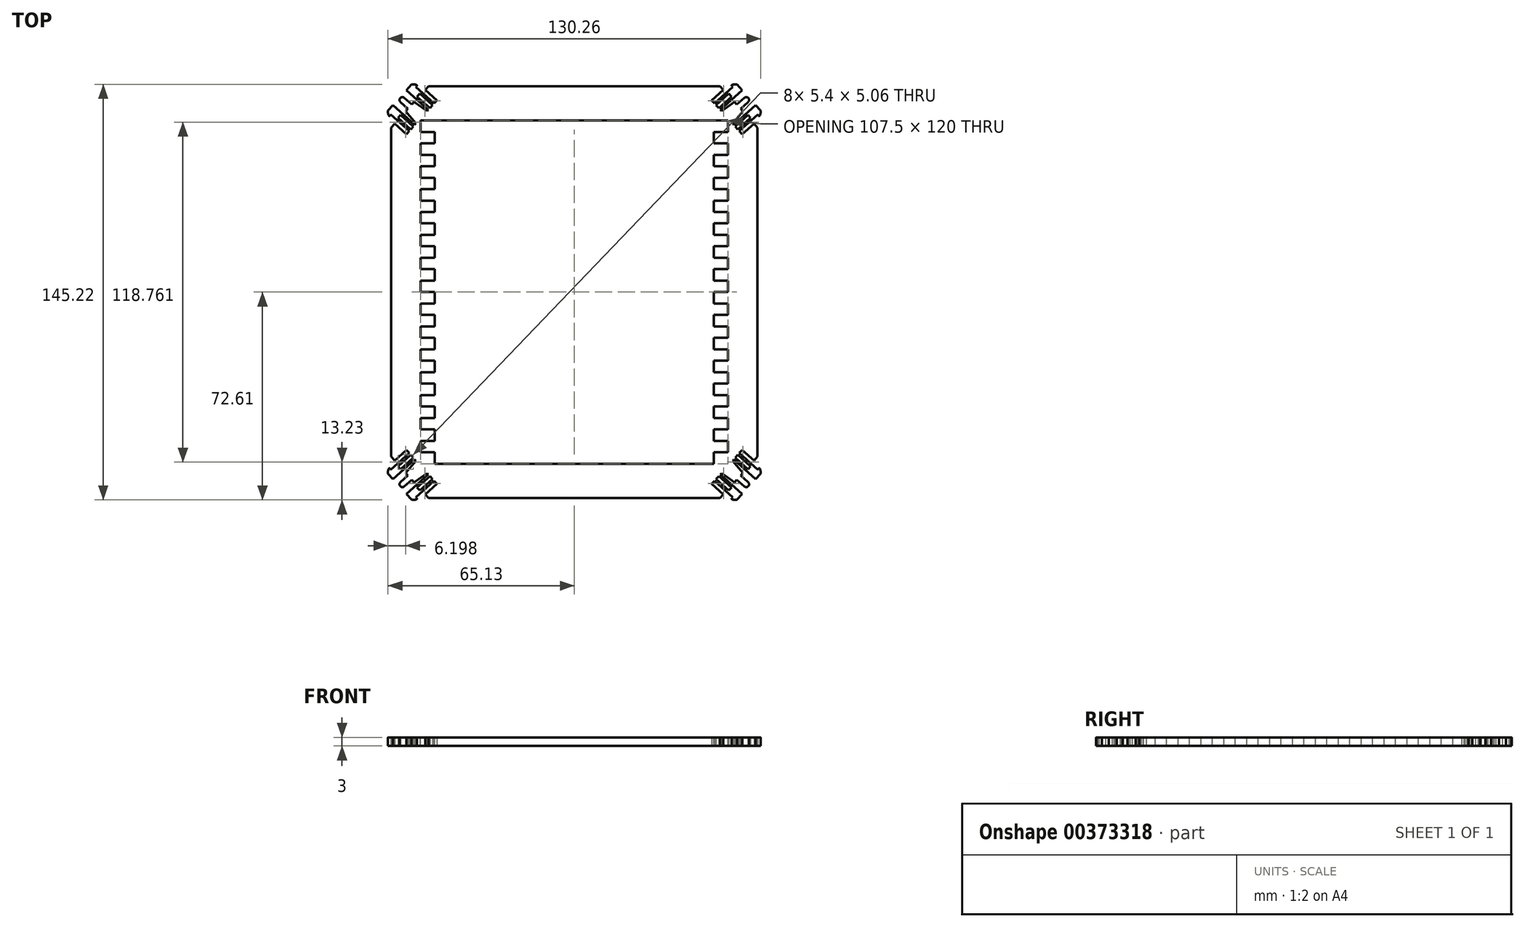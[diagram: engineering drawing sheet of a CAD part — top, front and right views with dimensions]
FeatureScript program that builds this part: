
annotation { "Feature Type Name" : "Feature", "Feature Type Description" : "" }
export const myFeature = defineFeature(function(context is Context, id is Id, definition is map)
    precondition{}
    {
        {
            var Q0;
            Q0=qCreatedBy(makeId("Top.planeOp"),FACE);
            var sketch = newSketch(context, id + "F0", { "sketchPlane" : qUnion([Q0])});
            skLineSegment(sketch, "E0", {"start": v(64, 57.49) * mm, "end": v(64, 0) * mm});
            skLineSegment(sketch, "E1", {"start": v(52.08, 70.72) * mm, "end": v(48, 67.04) * mm});
            skLineSegment(sketch, "E2", {"start": v(48, 67.04) * mm, "end": v(49, 65.92) * mm});
            skLineSegment(sketch, "E3", {"start": v(49, 65.92) * mm, "end": v(55.4, 71.67) * mm});
            skLineSegment(sketch, "E4", {"start": v(58.67, 70.58) * mm, "end": v(51.02, 63.69) * mm});
            skLineSegment(sketch, "E5", {"start": v(51.02, 63.69) * mm, "end": v(51.5, 63.29) * mm});
            skLineSegment(sketch, "E6", {"start": v(51.5, 63.29) * mm, "end": v(56, 66.46) * mm});
            skLineSegment(sketch, "E7", {"start": v(56, 66.46) * mm, "end": v(56.81, 65.55) * mm});
            skLineSegment(sketch, "E8", {"start": v(56.81, 65.55) * mm, "end": v(59.41, 67.89) * mm});
            skLineSegment(sketch, "E9", {"start": v(60.08, 67.15) * mm, "end": v(49.07, 57.23) * mm, "construction": true});
            skLineSegment(sketch, "E10.bottom", {"start": v(49.54, 65.32) * mm, "end": v(50.48, 64.28) * mm});
            skLineSegment(sketch, "E10.top", {"start": v(54, 69.34) * mm, "end": v(54.94, 68.3) * mm});
            skLineSegment(sketch, "E10.left", {"start": v(49.54, 65.32) * mm, "end": v(54, 69.34) * mm});
            skLineSegment(sketch, "E10.right", {"start": v(50.48, 64.28) * mm, "end": v(54.94, 68.3) * mm});
            skLineSegment(sketch, "E11", {"start": v(48, 67.04) * mm, "end": v(52.45, 62.1) * mm, "construction": true});
            skFitSpline(sketch, "E12", {"points": [v(55.4, 71.67) * mm, v(55, 72.26) * mm, v(56.93, 72.51) * mm], "startDerivative": vector(-1.28, 1.46) * mm, "endDerivative": vector(3.75, -1.07) * mm});
            skLineSegment(sketch, "E13", {"start": v(54.62, 75.08) * mm, "end": v(62.29, 66.57) * mm, "construction": true});
            skLineSegment(sketch, "E14", {"start": v(56.93, 72.51) * mm, "end": v(58.67, 70.58) * mm});
            skFitSpline(sketch, "E15.MirrorCS", {"points": [v(64.1, 62.01) * mm, v(64.64, 61.56) * mm, v(65.1, 63.45) * mm], "startDerivative": vector(1.32, -1.42) * mm, "endDerivative": vector(-0.67, 3.84) * mm});
            skLineSegment(sketch, "E16.MirrorCS", {"start": v(58.72, 55.14) * mm, "end": v(57.7, 56.26) * mm});
            skLineSegment(sketch, "E17.MirrorCS", {"start": v(57.17, 56.85) * mm, "end": v(56.23, 57.9) * mm});
            skLineSegment(sketch, "E18.MirrorCS", {"start": v(55.7, 58.49) * mm, "end": v(55.35, 59) * mm});
            skLineSegment(sketch, "E19.MirrorCS", {"start": v(58.72, 55.14) * mm, "end": v(54.27, 60.08) * mm, "construction": true});
            skLineSegment(sketch, "E20.MirrorCS", {"start": v(56.23, 57.9) * mm, "end": v(60.7, 61.9) * mm});
            skLineSegment(sketch, "E21.MirrorCS", {"start": v(62.8, 58.82) * mm, "end": v(58.72, 55.14) * mm});
            skLineSegment(sketch, "E22.MirrorCS", {"start": v(55.35, 59) * mm, "end": v(58.97, 63.15) * mm});
            skLineSegment(sketch, "E23.MirrorCS", {"start": v(63.35, 65.38) * mm, "end": v(55.7, 58.49) * mm});
            skLineSegment(sketch, "E24.MirrorCS", {"start": v(57.7, 56.26) * mm, "end": v(64.1, 62.01) * mm});
            skLineSegment(sketch, "E25.MirrorCS", {"start": v(65.1, 63.45) * mm, "end": v(63.35, 65.38) * mm});
            skLineSegment(sketch, "E26.MirrorCS", {"start": v(58.15, 64.06) * mm, "end": v(60.75, 66.4) * mm});
            skLineSegment(sketch, "E27.MirrorCS", {"start": v(61.63, 60.87) * mm, "end": v(60.7, 61.9) * mm});
            skLineSegment(sketch, "E28.MirrorCS", {"start": v(58.97, 63.15) * mm, "end": v(58.15, 64.06) * mm});
            skLineSegment(sketch, "E29.MirrorCS", {"start": v(57.17, 56.85) * mm, "end": v(61.63, 60.87) * mm});
            skArc(sketch, "E30", {"start": v(59.41, 67.89) * mm, "mid": v(60.83, 67.81) * mm, "end": v(60.75, 66.4) * mm});
            skLineSegment(sketch, "E31.0", {"start": v(54.62, 75.08) * mm, "end": v(56.93, 72.51) * mm, "construction": true});
            skLineSegment(sketch, "E32.0", {"start": v(51.5, 63.29) * mm, "end": v(52.45, 62.1) * mm, "construction": true});
            skLineSegment(sketch, "E33", {"start": v(50.93, 72) * mm, "end": v(0, 72) * mm});
            skLineSegment(sketch, "E34", {"start": v(0, 72) * mm, "end": v(0, 0) * mm});
            skLineSegment(sketch, "E35", {"start": v(0, 0) * mm, "end": v(64, 0) * mm});
            skLineSegment(sketch, "E36", {"start": v(52.08, 70.72) * mm, "end": v(50.93, 72) * mm});
            skLineSegment(sketch, "E37", {"start": v(62.8, 58.82) * mm, "end": v(64, 57.49) * mm});
            skSolve(sketch);
        }
        {
            var Q0;
            Q0=qSketchRegion(id+"F0",true);
            extrude(context, id + "F1", {"entities" : qUnion([Q0]), "depth" : 3 * mm});
        }
        {
            var Q0;
            Q0=makeQuery(id+"F1.opExtrude","SWEPT_BODY",BODY,{"disambiguationData":[OSD([sQuery(id+"F0.wireOp",EDGE,"E0"),sQuery(id+"F0.wireOp",EDGE,"E1"),sQuery(id+"F0.wireOp",EDGE,"E2"),sQuery(id+"F0.wireOp",EDGE,"E3"),sQuery(id+"F0.wireOp",EDGE,"E4"),sQuery(id+"F0.wireOp",EDGE,"E5"),sQuery(id+"F0.wireOp",EDGE,"E6"),sQuery(id+"F0.wireOp",EDGE,"E7"),sQuery(id+"F0.wireOp",EDGE,"E8"),sQuery(id+"F0.wireOp",EDGE,"E10.bottom"),sQuery(id+"F0.wireOp",EDGE,"E10.top"),sQuery(id+"F0.wireOp",EDGE,"E10.left"),sQuery(id+"F0.wireOp",EDGE,"E10.right"),sQuery(id+"F0.wireOp",EDGE,"E12"),sQuery(id+"F0.wireOp",EDGE,"E14"),sQuery(id+"F0.wireOp",EDGE,"E15.MirrorCS"),sQuery(id+"F0.wireOp",EDGE,"E16.MirrorCS"),sQuery(id+"F0.wireOp",EDGE,"E17.MirrorCS"),sQuery(id+"F0.wireOp",EDGE,"E18.MirrorCS"),sQuery(id+"F0.wireOp",EDGE,"73c64eb1-9053-4ded-a230-a61976290448.MirrorCS"),sQuery(id+"F0.wireOp",EDGE,"E20.MirrorCS"),sQuery(id+"F0.wireOp",EDGE,"E21.MirrorCS"),sQuery(id+"F0.wireOp",EDGE,"E22.MirrorCS"),sQuery(id+"F0.wireOp",EDGE,"E23.MirrorCS"),sQuery(id+"F0.wireOp",EDGE,"E24.MirrorCS"),sQuery(id+"F0.wireOp",EDGE,"E25.MirrorCS"),sQuery(id+"F0.wireOp",EDGE,"E26.MirrorCS"),sQuery(id+"F0.wireOp",EDGE,"E27.MirrorCS"),sQuery(id+"F0.wireOp",EDGE,"E28.MirrorCS"),sQuery(id+"F0.wireOp",EDGE,"E29.MirrorCS"),sQuery(id+"F0.wireOp",EDGE,"E30"),sQuery(id+"F0.wireOp",EDGE,"238d3171-18cf-4664-875a-15b81accc3c9"),sQuery(id+"F0.wireOp",EDGE,"7124a334-57a5-4c12-b1ba-874bc8632110.MirrorC"),sQuery(id+"F0.wireOp",EDGE,"E33"),sQuery(id+"F0.wireOp",EDGE,"44bece61-ac72-4aae-9b04-1ec5777349d3"),sQuery(id+"F0.wireOp",EDGE,"E34"),sQuery(id+"F0.wireOp",EDGE,"E35")])]});
            var Q1;
            Q1=makeQuery(id+"F1.opExtrude","SWEPT_FACE",FACE,{"disambiguationData":[OSD([sQuery(id+"F0.wireOp",EDGE,"E34")])]});
            mirror(context, id + "F2", {"operationType" : NewBodyOperationType.ADD, "entities" : qUnion([Q0]), "mirrorPlane" : qUnion([Q1])});
        }
        {
            var Q0;
            Q0=makeQuery(id+"F1.opExtrude","SWEPT_BODY",BODY,{"disambiguationData":[OSD([sQuery(id+"F0.wireOp",EDGE,"E0"),sQuery(id+"F0.wireOp",EDGE,"E1"),sQuery(id+"F0.wireOp",EDGE,"E2"),sQuery(id+"F0.wireOp",EDGE,"E3"),sQuery(id+"F0.wireOp",EDGE,"E4"),sQuery(id+"F0.wireOp",EDGE,"E5"),sQuery(id+"F0.wireOp",EDGE,"E6"),sQuery(id+"F0.wireOp",EDGE,"E7"),sQuery(id+"F0.wireOp",EDGE,"E8"),sQuery(id+"F0.wireOp",EDGE,"E10.bottom"),sQuery(id+"F0.wireOp",EDGE,"E10.top"),sQuery(id+"F0.wireOp",EDGE,"E10.left"),sQuery(id+"F0.wireOp",EDGE,"E10.right"),sQuery(id+"F0.wireOp",EDGE,"E12"),sQuery(id+"F0.wireOp",EDGE,"E14"),sQuery(id+"F0.wireOp",EDGE,"E15.MirrorCS"),sQuery(id+"F0.wireOp",EDGE,"E16.MirrorCS"),sQuery(id+"F0.wireOp",EDGE,"E17.MirrorCS"),sQuery(id+"F0.wireOp",EDGE,"E18.MirrorCS"),sQuery(id+"F0.wireOp",EDGE,"73c64eb1-9053-4ded-a230-a61976290448.MirrorCS"),sQuery(id+"F0.wireOp",EDGE,"E20.MirrorCS"),sQuery(id+"F0.wireOp",EDGE,"E21.MirrorCS"),sQuery(id+"F0.wireOp",EDGE,"E22.MirrorCS"),sQuery(id+"F0.wireOp",EDGE,"E23.MirrorCS"),sQuery(id+"F0.wireOp",EDGE,"E24.MirrorCS"),sQuery(id+"F0.wireOp",EDGE,"E25.MirrorCS"),sQuery(id+"F0.wireOp",EDGE,"E26.MirrorCS"),sQuery(id+"F0.wireOp",EDGE,"E27.MirrorCS"),sQuery(id+"F0.wireOp",EDGE,"E28.MirrorCS"),sQuery(id+"F0.wireOp",EDGE,"E29.MirrorCS"),sQuery(id+"F0.wireOp",EDGE,"E30"),sQuery(id+"F0.wireOp",EDGE,"238d3171-18cf-4664-875a-15b81accc3c9"),sQuery(id+"F0.wireOp",EDGE,"7124a334-57a5-4c12-b1ba-874bc8632110.MirrorC"),sQuery(id+"F0.wireOp",EDGE,"E33"),sQuery(id+"F0.wireOp",EDGE,"44bece61-ac72-4aae-9b04-1ec5777349d3"),sQuery(id+"F0.wireOp",EDGE,"E34"),sQuery(id+"F0.wireOp",EDGE,"E35")])]});
            var Q1;
            {var subQ0=makeQuery(id+"F1.opExtrude","SWEPT_FACE",FACE,{"disambiguationData":[OSD([sQuery(id+"F0.wireOp",EDGE,"E35")])]});Q1=makeQuery(id+"F2.boolean.opBoolean","MERGE",FACE,{"derivedFrom":[subQ0,makeQuery(id+"F2.opPattern","COPY",FACE,{"derivedFrom":subQ0,"instanceName":"1"})]});}
            mirror(context, id + "F3", {"operationType" : NewBodyOperationType.ADD, "entities" : qUnion([Q0]), "mirrorPlane" : qUnion([Q1])});
        }
        {
            var Q0;
            {var subQ0=makeQuery(id+"F1.opExtrude","CAP_FACE",FACE,{"disambiguationData":[OSD([sQuery(id+"F0.wireOp",EDGE,"E0"),sQuery(id+"F0.wireOp",EDGE,"E1"),sQuery(id+"F0.wireOp",EDGE,"E2"),sQuery(id+"F0.wireOp",EDGE,"E3"),sQuery(id+"F0.wireOp",EDGE,"E4"),sQuery(id+"F0.wireOp",EDGE,"E5"),sQuery(id+"F0.wireOp",EDGE,"E6"),sQuery(id+"F0.wireOp",EDGE,"E7"),sQuery(id+"F0.wireOp",EDGE,"E8"),sQuery(id+"F0.wireOp",EDGE,"E10.bottom"),sQuery(id+"F0.wireOp",EDGE,"E10.top"),sQuery(id+"F0.wireOp",EDGE,"E10.left"),sQuery(id+"F0.wireOp",EDGE,"E10.right"),sQuery(id+"F0.wireOp",EDGE,"E12"),sQuery(id+"F0.wireOp",EDGE,"E14"),sQuery(id+"F0.wireOp",EDGE,"E15.MirrorCS"),sQuery(id+"F0.wireOp",EDGE,"E16.MirrorCS"),sQuery(id+"F0.wireOp",EDGE,"E17.MirrorCS"),sQuery(id+"F0.wireOp",EDGE,"E18.MirrorCS"),sQuery(id+"F0.wireOp",EDGE,"73c64eb1-9053-4ded-a230-a61976290448.MirrorCS"),sQuery(id+"F0.wireOp",EDGE,"E20.MirrorCS"),sQuery(id+"F0.wireOp",EDGE,"E21.MirrorCS"),sQuery(id+"F0.wireOp",EDGE,"E22.MirrorCS"),sQuery(id+"F0.wireOp",EDGE,"E23.MirrorCS"),sQuery(id+"F0.wireOp",EDGE,"E24.MirrorCS"),sQuery(id+"F0.wireOp",EDGE,"E25.MirrorCS"),sQuery(id+"F0.wireOp",EDGE,"E26.MirrorCS"),sQuery(id+"F0.wireOp",EDGE,"E27.MirrorCS"),sQuery(id+"F0.wireOp",EDGE,"E28.MirrorCS"),sQuery(id+"F0.wireOp",EDGE,"E29.MirrorCS"),sQuery(id+"F0.wireOp",EDGE,"E30"),sQuery(id+"F0.wireOp",EDGE,"238d3171-18cf-4664-875a-15b81accc3c9"),sQuery(id+"F0.wireOp",EDGE,"7124a334-57a5-4c12-b1ba-874bc8632110.MirrorC"),sQuery(id+"F0.wireOp",EDGE,"E33"),sQuery(id+"F0.wireOp",EDGE,"44bece61-ac72-4aae-9b04-1ec5777349d3"),sQuery(id+"F0.wireOp",EDGE,"E34"),sQuery(id+"F0.wireOp",EDGE,"E35")])],"isStart":false});var subQ1=makeQuery(id+"F2.boolean.opBoolean","MERGE",FACE,{"derivedFrom":[subQ0,makeQuery(id+"F2.opPattern","COPY",FACE,{"derivedFrom":subQ0,"instanceName":"1"})]});Q0=makeQuery(id+"F3.boolean.opBoolean","MERGE",FACE,{"derivedFrom":[subQ1,makeQuery(id+"F3.opPattern","COPY",FACE,{"derivedFrom":subQ1,"instanceName":"1"})]});}
            var sketch = newSketch(context, id + "F4", { "sketchPlane" : qUnion([Q0])});
            skLineSegment(sketch, "E38.bottom", {"start": v(53.75, 60) * mm, "end": v(-53.75, 60) * mm});
            skLineSegment(sketch, "E38.top", {"start": v(53.75, -60) * mm, "end": v(-53.75, -60) * mm});
            skLineSegment(sketch, "E38.left", {"start": v(53.75, 60) * mm, "end": v(53.75, -60) * mm});
            skLineSegment(sketch, "E38.right", {"start": v(-53.75, 60) * mm, "end": v(-53.75, -60) * mm});
            skPoint(sketch, "E38.middle", {"position": v(0, 0) * mm});
            skSolve(sketch);
        }
        {
            var Q0;
            Q0=qSketchRegion(id+"F4",true);
            extrude(context, id + "F5", {"entities" : qUnion([Q0]), "operationType" : NewBodyOperationType.REMOVE, "oppositeDirection" : true, "depth" : 3 * mm});
        }
        {
            var Q0;
            {var subQ0=makeQuery(id+"F1.opExtrude","CAP_FACE",FACE,{"disambiguationData":[OSD([sQuery(id+"F0.wireOp",EDGE,"E0"),sQuery(id+"F0.wireOp",EDGE,"E1"),sQuery(id+"F0.wireOp",EDGE,"E2"),sQuery(id+"F0.wireOp",EDGE,"E3"),sQuery(id+"F0.wireOp",EDGE,"E4"),sQuery(id+"F0.wireOp",EDGE,"E5"),sQuery(id+"F0.wireOp",EDGE,"E6"),sQuery(id+"F0.wireOp",EDGE,"E7"),sQuery(id+"F0.wireOp",EDGE,"E8"),sQuery(id+"F0.wireOp",EDGE,"E10.bottom"),sQuery(id+"F0.wireOp",EDGE,"E10.top"),sQuery(id+"F0.wireOp",EDGE,"E10.left"),sQuery(id+"F0.wireOp",EDGE,"E10.right"),sQuery(id+"F0.wireOp",EDGE,"E12"),sQuery(id+"F0.wireOp",EDGE,"E14"),sQuery(id+"F0.wireOp",EDGE,"E15.MirrorCS"),sQuery(id+"F0.wireOp",EDGE,"E16.MirrorCS"),sQuery(id+"F0.wireOp",EDGE,"E17.MirrorCS"),sQuery(id+"F0.wireOp",EDGE,"E18.MirrorCS"),sQuery(id+"F0.wireOp",EDGE,"E20.MirrorCS"),sQuery(id+"F0.wireOp",EDGE,"E21.MirrorCS"),sQuery(id+"F0.wireOp",EDGE,"E22.MirrorCS"),sQuery(id+"F0.wireOp",EDGE,"E23.MirrorCS"),sQuery(id+"F0.wireOp",EDGE,"E24.MirrorCS"),sQuery(id+"F0.wireOp",EDGE,"E25.MirrorCS"),sQuery(id+"F0.wireOp",EDGE,"E26.MirrorCS"),sQuery(id+"F0.wireOp",EDGE,"E27.MirrorCS"),sQuery(id+"F0.wireOp",EDGE,"E28.MirrorCS"),sQuery(id+"F0.wireOp",EDGE,"E29.MirrorCS"),sQuery(id+"F0.wireOp",EDGE,"E30"),sQuery(id+"F0.wireOp",EDGE,"238d3171-18cf-4664-875a-15b81accc3c9"),sQuery(id+"F0.wireOp",EDGE,"7124a334-57a5-4c12-b1ba-874bc8632110.MirrorC"),sQuery(id+"F0.wireOp",EDGE,"E33"),sQuery(id+"F0.wireOp",EDGE,"E34"),sQuery(id+"F0.wireOp",EDGE,"E35"),sQuery(id+"F0.wireOp",EDGE,"E36"),sQuery(id+"F0.wireOp",EDGE,"E37")])],"isStart":false});var subQ1=makeQuery(id+"F2.boolean.opBoolean","MERGE",FACE,{"derivedFrom":[subQ0,makeQuery(id+"F2.opPattern","COPY",FACE,{"derivedFrom":subQ0,"instanceName":"1"})]});Q0=makeQuery(id+"F3.boolean.opBoolean","MERGE",FACE,{"derivedFrom":[subQ1,makeQuery(id+"F3.opPattern","COPY",FACE,{"derivedFrom":subQ1,"instanceName":"1"})]});}
            var sketch = newSketch(context, id + "F6", { "sketchPlane" : qUnion([Q0])});
            skPoint(sketch, "E39.middle", {"position": v(0, 0) * mm});
            skLineSegment(sketch, "E40.bottom", {"start": v(-53.75, -60) * mm, "end": v(-48.75, -60) * mm});
            skLineSegment(sketch, "E40.top", {"start": v(-53.75, -56) * mm, "end": v(-48.75, -56) * mm});
            skLineSegment(sketch, "E40.left", {"start": v(-53.75, -60) * mm, "end": v(-53.75, -56) * mm});
            skLineSegment(sketch, "E40.right", {"start": v(-48.75, -60) * mm, "end": v(-48.75, -56) * mm});
            skLineSegment(sketch, "E41.0.1.0", {"start": v(-48.75, -52) * mm, "end": v(-48.75, -48) * mm});
            skLineSegment(sketch, "E41.0.1.1", {"start": v(-53.75, -48) * mm, "end": v(-48.75, -48) * mm});
            skLineSegment(sketch, "E41.0.1.2", {"start": v(-53.75, -52) * mm, "end": v(-53.75, -48) * mm});
            skLineSegment(sketch, "E41.0.1.3", {"start": v(-53.75, -52) * mm, "end": v(-48.75, -52) * mm});
            skLineSegment(sketch, "E41.0.2.0", {"start": v(-48.75, -44) * mm, "end": v(-48.75, -40) * mm});
            skLineSegment(sketch, "E41.0.2.1", {"start": v(-53.75, -40) * mm, "end": v(-48.75, -40) * mm});
            skLineSegment(sketch, "E41.0.2.2", {"start": v(-53.75, -44) * mm, "end": v(-53.75, -40) * mm});
            skLineSegment(sketch, "E41.0.2.3", {"start": v(-53.75, -44) * mm, "end": v(-48.75, -44) * mm});
            skLineSegment(sketch, "E41.0.3.0", {"start": v(-48.75, -36) * mm, "end": v(-48.75, -32) * mm});
            skLineSegment(sketch, "E41.0.3.1", {"start": v(-53.75, -32) * mm, "end": v(-48.75, -32) * mm});
            skLineSegment(sketch, "E41.0.3.2", {"start": v(-53.75, -36) * mm, "end": v(-53.75, -32) * mm});
            skLineSegment(sketch, "E41.0.3.3", {"start": v(-53.75, -36) * mm, "end": v(-48.75, -36) * mm});
            skLineSegment(sketch, "E41.0.4.0", {"start": v(-48.75, -28) * mm, "end": v(-48.75, -24) * mm});
            skLineSegment(sketch, "E41.0.4.1", {"start": v(-53.75, -24) * mm, "end": v(-48.75, -24) * mm});
            skLineSegment(sketch, "E41.0.4.2", {"start": v(-53.75, -28) * mm, "end": v(-53.75, -24) * mm});
            skLineSegment(sketch, "E41.0.4.3", {"start": v(-53.75, -28) * mm, "end": v(-48.75, -28) * mm});
            skLineSegment(sketch, "E41.0.5.0", {"start": v(-48.75, -20) * mm, "end": v(-48.75, -16) * mm});
            skLineSegment(sketch, "E41.0.5.1", {"start": v(-53.75, -16) * mm, "end": v(-48.75, -16) * mm});
            skLineSegment(sketch, "E41.0.5.2", {"start": v(-53.75, -20) * mm, "end": v(-53.75, -16) * mm});
            skLineSegment(sketch, "E41.0.5.3", {"start": v(-53.75, -20) * mm, "end": v(-48.75, -20) * mm});
            skLineSegment(sketch, "E41.0.6.0", {"start": v(-48.75, -12) * mm, "end": v(-48.75, -8) * mm});
            skLineSegment(sketch, "E41.0.6.1", {"start": v(-53.75, -8) * mm, "end": v(-48.75, -8) * mm});
            skLineSegment(sketch, "E41.0.6.2", {"start": v(-53.75, -12) * mm, "end": v(-53.75, -8) * mm});
            skLineSegment(sketch, "E41.0.6.3", {"start": v(-53.75, -12) * mm, "end": v(-48.75, -12) * mm});
            skLineSegment(sketch, "E41.0.7.0", {"start": v(-48.75, -4) * mm, "end": v(-48.75, 0) * mm});
            skLineSegment(sketch, "E41.0.7.1", {"start": v(-53.75, 0) * mm, "end": v(-48.75, 0) * mm});
            skLineSegment(sketch, "E41.0.7.2", {"start": v(-53.75, -4) * mm, "end": v(-53.75, 0) * mm});
            skLineSegment(sketch, "E41.0.7.3", {"start": v(-53.75, -4) * mm, "end": v(-48.75, -4) * mm});
            skLineSegment(sketch, "E41.0.8.0", {"start": v(-48.75, 4) * mm, "end": v(-48.75, 8) * mm});
            skLineSegment(sketch, "E41.0.8.1", {"start": v(-53.75, 8) * mm, "end": v(-48.75, 8) * mm});
            skLineSegment(sketch, "E41.0.8.2", {"start": v(-53.75, 4) * mm, "end": v(-53.75, 8) * mm});
            skLineSegment(sketch, "E41.0.8.3", {"start": v(-53.75, 4) * mm, "end": v(-48.75, 4) * mm});
            skLineSegment(sketch, "E41.0.9.0", {"start": v(-48.75, 12) * mm, "end": v(-48.75, 16) * mm});
            skLineSegment(sketch, "E41.0.9.1", {"start": v(-53.75, 16) * mm, "end": v(-48.75, 16) * mm});
            skLineSegment(sketch, "E41.0.9.2", {"start": v(-53.75, 12) * mm, "end": v(-53.75, 16) * mm});
            skLineSegment(sketch, "E41.0.9.3", {"start": v(-53.75, 12) * mm, "end": v(-48.75, 12) * mm});
            skLineSegment(sketch, "E41.0.10.0", {"start": v(-48.75, 20) * mm, "end": v(-48.75, 24) * mm});
            skLineSegment(sketch, "E41.0.10.1", {"start": v(-53.75, 24) * mm, "end": v(-48.75, 24) * mm});
            skLineSegment(sketch, "E41.0.10.2", {"start": v(-53.75, 20) * mm, "end": v(-53.75, 24) * mm});
            skLineSegment(sketch, "E41.0.10.3", {"start": v(-53.75, 20) * mm, "end": v(-48.75, 20) * mm});
            skLineSegment(sketch, "E41.0.11.0", {"start": v(-48.75, 28) * mm, "end": v(-48.75, 32) * mm});
            skLineSegment(sketch, "E41.0.11.1", {"start": v(-53.75, 32) * mm, "end": v(-48.75, 32) * mm});
            skLineSegment(sketch, "E41.0.11.2", {"start": v(-53.75, 28) * mm, "end": v(-53.75, 32) * mm});
            skLineSegment(sketch, "E41.0.11.3", {"start": v(-53.75, 28) * mm, "end": v(-48.75, 28) * mm});
            skLineSegment(sketch, "E41.0.12.0", {"start": v(-48.75, 36) * mm, "end": v(-48.75, 40) * mm});
            skLineSegment(sketch, "E41.0.12.1", {"start": v(-53.75, 40) * mm, "end": v(-48.75, 40) * mm});
            skLineSegment(sketch, "E41.0.12.2", {"start": v(-53.75, 36) * mm, "end": v(-53.75, 40) * mm});
            skLineSegment(sketch, "E41.0.12.3", {"start": v(-53.75, 36) * mm, "end": v(-48.75, 36) * mm});
            skLineSegment(sketch, "E41.0.13.0", {"start": v(-48.75, 44) * mm, "end": v(-48.75, 48) * mm});
            skLineSegment(sketch, "E41.0.13.1", {"start": v(-53.75, 48) * mm, "end": v(-48.75, 48) * mm});
            skLineSegment(sketch, "E41.0.13.2", {"start": v(-53.75, 44) * mm, "end": v(-53.75, 48) * mm});
            skLineSegment(sketch, "E41.0.13.3", {"start": v(-53.75, 44) * mm, "end": v(-48.75, 44) * mm});
            skLineSegment(sketch, "E41.0.14.0", {"start": v(-48.75, 52) * mm, "end": v(-48.75, 56) * mm});
            skLineSegment(sketch, "E41.0.14.1", {"start": v(-53.75, 56) * mm, "end": v(-48.75, 56) * mm});
            skLineSegment(sketch, "E41.0.14.2", {"start": v(-53.75, 52) * mm, "end": v(-53.75, 56) * mm});
            skLineSegment(sketch, "E41.0.14.3", {"start": v(-53.75, 52) * mm, "end": v(-48.75, 52) * mm});
            skLineSegment(sketch, "E41.1.0.0", {"start": v(53.75, -60) * mm, "end": v(53.75, -56) * mm});
            skLineSegment(sketch, "E41.1.0.1", {"start": v(48.75, -56) * mm, "end": v(53.75, -56) * mm});
            skLineSegment(sketch, "E41.1.0.2", {"start": v(48.75, -60) * mm, "end": v(48.75, -56) * mm});
            skLineSegment(sketch, "E41.1.0.3", {"start": v(48.75, -60) * mm, "end": v(53.75, -60) * mm});
            skLineSegment(sketch, "E41.1.1.0", {"start": v(53.75, -52) * mm, "end": v(53.75, -48) * mm});
            skLineSegment(sketch, "E41.1.1.1", {"start": v(48.75, -48) * mm, "end": v(53.75, -48) * mm});
            skLineSegment(sketch, "E41.1.1.2", {"start": v(48.75, -52) * mm, "end": v(48.75, -48) * mm});
            skLineSegment(sketch, "E41.1.1.3", {"start": v(48.75, -52) * mm, "end": v(53.75, -52) * mm});
            skLineSegment(sketch, "E41.1.2.0", {"start": v(53.75, -44) * mm, "end": v(53.75, -40) * mm});
            skLineSegment(sketch, "E41.1.2.1", {"start": v(48.75, -40) * mm, "end": v(53.75, -40) * mm});
            skLineSegment(sketch, "E41.1.2.2", {"start": v(48.75, -44) * mm, "end": v(48.75, -40) * mm});
            skLineSegment(sketch, "E41.1.2.3", {"start": v(48.75, -44) * mm, "end": v(53.75, -44) * mm});
            skLineSegment(sketch, "E41.1.3.0", {"start": v(53.75, -36) * mm, "end": v(53.75, -32) * mm});
            skLineSegment(sketch, "E41.1.3.1", {"start": v(48.75, -32) * mm, "end": v(53.75, -32) * mm});
            skLineSegment(sketch, "E41.1.3.2", {"start": v(48.75, -36) * mm, "end": v(48.75, -32) * mm});
            skLineSegment(sketch, "E41.1.3.3", {"start": v(48.75, -36) * mm, "end": v(53.75, -36) * mm});
            skLineSegment(sketch, "E41.1.4.0", {"start": v(53.75, -28) * mm, "end": v(53.75, -24) * mm});
            skLineSegment(sketch, "E41.1.4.1", {"start": v(48.75, -24) * mm, "end": v(53.75, -24) * mm});
            skLineSegment(sketch, "E41.1.4.2", {"start": v(48.75, -28) * mm, "end": v(48.75, -24) * mm});
            skLineSegment(sketch, "E41.1.4.3", {"start": v(48.75, -28) * mm, "end": v(53.75, -28) * mm});
            skLineSegment(sketch, "E41.1.5.0", {"start": v(53.75, -20) * mm, "end": v(53.75, -16) * mm});
            skLineSegment(sketch, "E41.1.5.1", {"start": v(48.75, -16) * mm, "end": v(53.75, -16) * mm});
            skLineSegment(sketch, "E41.1.5.2", {"start": v(48.75, -20) * mm, "end": v(48.75, -16) * mm});
            skLineSegment(sketch, "E41.1.5.3", {"start": v(48.75, -20) * mm, "end": v(53.75, -20) * mm});
            skLineSegment(sketch, "E41.1.6.0", {"start": v(53.75, -12) * mm, "end": v(53.75, -8) * mm});
            skLineSegment(sketch, "E41.1.6.1", {"start": v(48.75, -8) * mm, "end": v(53.75, -8) * mm});
            skLineSegment(sketch, "E41.1.6.2", {"start": v(48.75, -12) * mm, "end": v(48.75, -8) * mm});
            skLineSegment(sketch, "E41.1.6.3", {"start": v(48.75, -12) * mm, "end": v(53.75, -12) * mm});
            skLineSegment(sketch, "E41.1.7.0", {"start": v(53.75, -4) * mm, "end": v(53.75, 0) * mm});
            skLineSegment(sketch, "E41.1.7.1", {"start": v(48.75, 0) * mm, "end": v(53.75, 0) * mm});
            skLineSegment(sketch, "E41.1.7.2", {"start": v(48.75, -4) * mm, "end": v(48.75, 0) * mm});
            skLineSegment(sketch, "E41.1.7.3", {"start": v(48.75, -4) * mm, "end": v(53.75, -4) * mm});
            skLineSegment(sketch, "E41.1.8.0", {"start": v(53.75, 4) * mm, "end": v(53.75, 8) * mm});
            skLineSegment(sketch, "E41.1.8.1", {"start": v(48.75, 8) * mm, "end": v(53.75, 8) * mm});
            skLineSegment(sketch, "E41.1.8.2", {"start": v(48.75, 4) * mm, "end": v(48.75, 8) * mm});
            skLineSegment(sketch, "E41.1.8.3", {"start": v(48.75, 4) * mm, "end": v(53.75, 4) * mm});
            skLineSegment(sketch, "E41.1.9.0", {"start": v(53.75, 12) * mm, "end": v(53.75, 16) * mm});
            skLineSegment(sketch, "E41.1.9.1", {"start": v(48.75, 16) * mm, "end": v(53.75, 16) * mm});
            skLineSegment(sketch, "E41.1.9.2", {"start": v(48.75, 12) * mm, "end": v(48.75, 16) * mm});
            skLineSegment(sketch, "E41.1.9.3", {"start": v(48.75, 12) * mm, "end": v(53.75, 12) * mm});
            skLineSegment(sketch, "E41.1.10.0", {"start": v(53.75, 20) * mm, "end": v(53.75, 24) * mm});
            skLineSegment(sketch, "E41.1.10.1", {"start": v(48.75, 24) * mm, "end": v(53.75, 24) * mm});
            skLineSegment(sketch, "E41.1.10.2", {"start": v(48.75, 20) * mm, "end": v(48.75, 24) * mm});
            skLineSegment(sketch, "E41.1.10.3", {"start": v(48.75, 20) * mm, "end": v(53.75, 20) * mm});
            skLineSegment(sketch, "E41.1.11.0", {"start": v(53.75, 28) * mm, "end": v(53.75, 32) * mm});
            skLineSegment(sketch, "E41.1.11.1", {"start": v(48.75, 32) * mm, "end": v(53.75, 32) * mm});
            skLineSegment(sketch, "E41.1.11.2", {"start": v(48.75, 28) * mm, "end": v(48.75, 32) * mm});
            skLineSegment(sketch, "E41.1.11.3", {"start": v(48.75, 28) * mm, "end": v(53.75, 28) * mm});
            skLineSegment(sketch, "E41.1.12.0", {"start": v(53.75, 36) * mm, "end": v(53.75, 40) * mm});
            skLineSegment(sketch, "E41.1.12.1", {"start": v(48.75, 40) * mm, "end": v(53.75, 40) * mm});
            skLineSegment(sketch, "E41.1.12.2", {"start": v(48.75, 36) * mm, "end": v(48.75, 40) * mm});
            skLineSegment(sketch, "E41.1.12.3", {"start": v(48.75, 36) * mm, "end": v(53.75, 36) * mm});
            skLineSegment(sketch, "E41.1.13.0", {"start": v(53.75, 44) * mm, "end": v(53.75, 48) * mm});
            skLineSegment(sketch, "E41.1.13.1", {"start": v(48.75, 48) * mm, "end": v(53.75, 48) * mm});
            skLineSegment(sketch, "E41.1.13.2", {"start": v(48.75, 44) * mm, "end": v(48.75, 48) * mm});
            skLineSegment(sketch, "E41.1.13.3", {"start": v(48.75, 44) * mm, "end": v(53.75, 44) * mm});
            skLineSegment(sketch, "E41.1.14.0", {"start": v(53.75, 52) * mm, "end": v(53.75, 56) * mm});
            skLineSegment(sketch, "E41.1.14.1", {"start": v(48.75, 56) * mm, "end": v(53.75, 56) * mm});
            skLineSegment(sketch, "E41.1.14.2", {"start": v(48.75, 52) * mm, "end": v(48.75, 56) * mm});
            skLineSegment(sketch, "E41.1.14.3", {"start": v(48.75, 52) * mm, "end": v(53.75, 52) * mm});
            skLineSegment(sketch, "E41.direction1", {"start": v(-53.75, -60) * mm, "end": v(48.75, -60) * mm, "construction": true});
            skLineSegment(sketch, "E41.direction2", {"start": v(-53.75, -60) * mm, "end": v(-53.75, -52) * mm, "construction": true});
            skSolve(sketch);
        }
        {
            var Q0;
            Q0=qSketchRegion(id+"F6",true);
            extrude(context, id + "F7", {"entities" : qUnion([Q0]), "operationType" : NewBodyOperationType.ADD, "oppositeDirection" : true, "depth" : 3 * mm});
        }
    });
